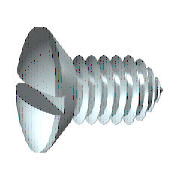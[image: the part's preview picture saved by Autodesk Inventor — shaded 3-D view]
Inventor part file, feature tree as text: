
AUTODESK INVENTOR PART (.ipt)
format: ipt  version: 2020 (Build 240168000, 168)  size: 173,056 bytes
history: native  units: mm (DEFAULTED — no unit token found)
features: sketch x2, other x1, extrude x1, plane x1
ambient origin geometry x8: Origin, YZ Plane, XZ Plane, XY Plane, X Axis, Y Axis, Z Axis, Center Point
bodies: Solid1 (feature_tree), Body (feature_tree)
feature tree (5):
  other  "IDS_WORKPLANE{1}"
  extrude  "Slot"  Depth=3.5mm
  plane  "Work Plane2"
  sketch  "Sketch1"  dims[d0=0.8mm d1=3.5mm]
  sketch  "Sketch2"  dims[d2=7.3mm d17=90.0deg d3=10.65mm d4=0.0mm d5=1.75mm d6=3.2mm d7=-0.8mm d8=1.0mm d9=1.4mm d10=0.0mm d11=45.0deg d14=2.35mm d15=10.65mm d16=0.0mm d38=45.0deg d41=0.0mm d42=0.0mm]
